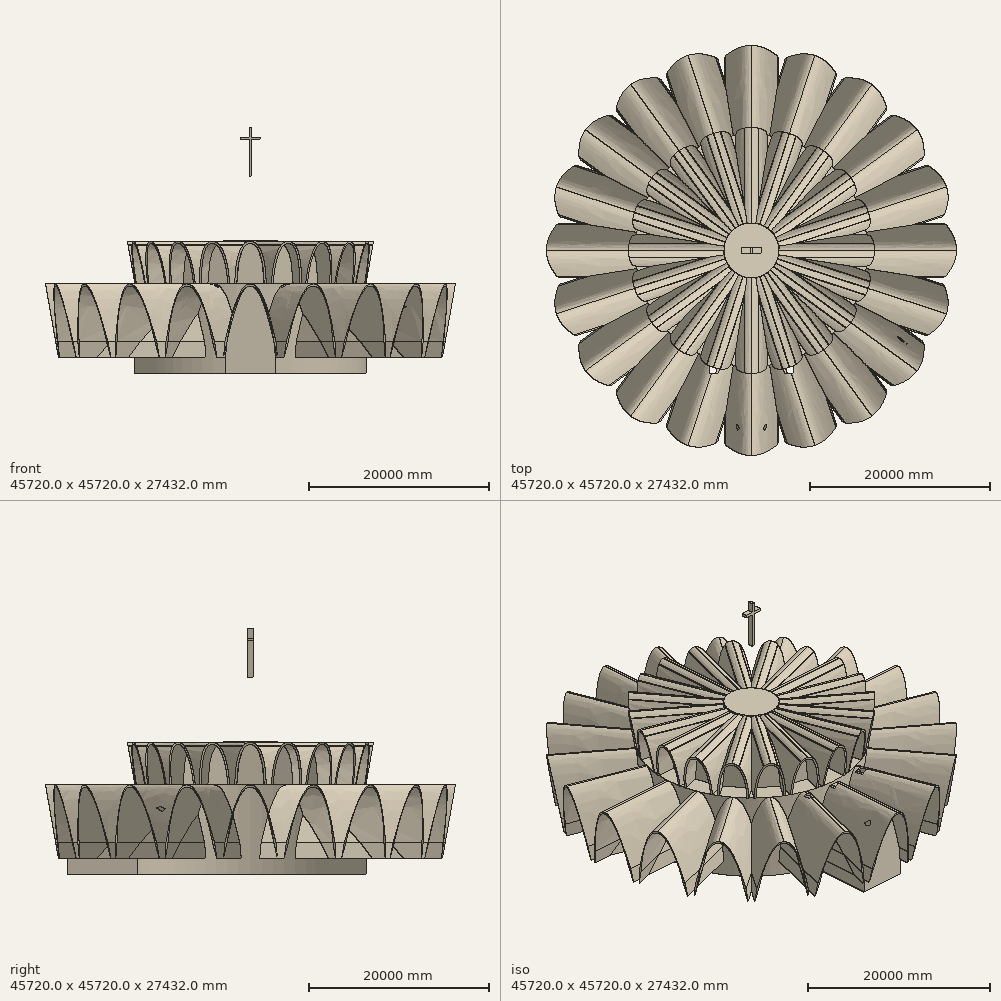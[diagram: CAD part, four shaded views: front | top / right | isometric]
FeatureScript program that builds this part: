
annotation { "Feature Type Name" : "Feature", "Feature Type Description" : "" }
export const myFeature = defineFeature(function(context is Context, id is Id, definition is map)
    precondition{}
    {
        {
            var Q0;
            Q0=qCreatedBy(makeId("Front.planeOp"),FACE);
            var sketch = newSketch(context, id + "F0", { "sketchPlane" : qUnion([Q0])});
            skFitSpline(sketch, "E0", {"points": [v(-2819.4, 0.59) * mm, v(0, 9753.6) * mm, v(3431.03, -271.27) * mm], "startDerivative": vector(-180.02, 33749.09) * mm, "endDerivative": vector(6673.33, -32256.88) * mm});
            skLineSegment(sketch, "E1", {"start": v(0, 0) * mm, "end": v(0, 27432) * mm, "construction": true});
            skFitSpline(sketch, "E2.MirrorCS", {"points": [v(2819.4, 0.59) * mm, v(0, 9753.6) * mm, v(-3431.03, -271.27) * mm], "startDerivative": vector(180.02, 33749.09) * mm, "endDerivative": vector(-6673.33, -32256.88) * mm});
            skLineSegment(sketch, "E3", {"start": v(-1350.09, 27432) * mm, "end": v(1344.94, 27432) * mm, "construction": true});
            skFitSpline(sketch, "E4", {"points": [v(-1524, 9982.83) * mm, v(0, 14487.94) * mm], "startDerivative": vector(0, 6892.9) * mm, "endDerivative": vector(3021.33, 0) * mm});
            skFitSpline(sketch, "E5.MirrorCS", {"points": [v(1524, 9982.83) * mm, v(0, 14487.94) * mm], "startDerivative": vector(0, 6892.9) * mm, "endDerivative": vector(-3021.33, 0) * mm});
            skLineSegment(sketch, "E6", {"start": v(-23096.64, 7972.17) * mm, "end": v(22623.36, 7972.17) * mm, "construction": true});
            skLineSegment(sketch, "E7", {"start": v(-158.94, 27432) * mm, "end": v(-158.94, 26322.91) * mm});
            skLineSegment(sketch, "E8", {"start": v(-158.94, 26322.91) * mm, "end": v(-1101.37, 26322.91) * mm});
            skLineSegment(sketch, "E9", {"start": v(-1101.37, 26322.91) * mm, "end": v(-1101.37, 26041.27) * mm});
            skLineSegment(sketch, "E10", {"start": v(-1101.37, 26041.27) * mm, "end": v(-158.94, 26041.27) * mm});
            skLineSegment(sketch, "E11", {"start": v(-158.94, 26041.27) * mm, "end": v(-158.94, 22529.93) * mm});
            skLineSegment(sketch, "E12.MirrorCS", {"start": v(158.94, 27432) * mm, "end": v(158.94, 26322.91) * mm});
            skLineSegment(sketch, "E13.MirrorCS", {"start": v(158.94, 26322.91) * mm, "end": v(1101.37, 26322.91) * mm});
            skLineSegment(sketch, "E14.MirrorCS", {"start": v(1101.37, 26041.27) * mm, "end": v(158.94, 26041.27) * mm});
            skLineSegment(sketch, "E15.MirrorCS", {"start": v(1101.37, 26322.91) * mm, "end": v(1101.37, 26041.27) * mm});
            skLineSegment(sketch, "E16.MirrorCS", {"start": v(158.94, 26041.27) * mm, "end": v(158.94, 22529.93) * mm});
            skLineSegment(sketch, "E17", {"start": v(-158.94, 27432) * mm, "end": v(0, 27432) * mm});
            skLineSegment(sketch, "E18", {"start": v(0, 27432) * mm, "end": v(158.94, 27432) * mm});
            skFitSpline(sketch, "E19.0", {"points": [v(-3048, -0.63) * mm, v(-3049.89, 353.68) * mm, v(-3040.8, 1051.7) * mm, v(-2991.4, 2062.48) * mm, v(-2909.12, 3032.6) * mm, v(-2796.79, 3957.69) * mm, v(-2657.24, 4833.35) * mm, v(-2493.26, 5655.25) * mm, v(-2307.6, 6419.11) * mm, v(-2137.06, 7003.78) * mm, v(-1992.4, 7438.35) * mm, v(-1880.08, 7747.2) * mm, v(-1764.24, 8038.47) * mm, v(-1645.12, 8311.72) * mm, v(-1522.95, 8566.49) * mm, v(-1397.88, 8802.35) * mm, v(-1270.03, 9018.9) * mm, v(-1161.14, 9182.94) * mm, v(-1072.55, 9304.14) * mm, v(-1005.32, 9389.97) * mm, v(-937.25, 9470.68) * mm, v(-868.26, 9546.2) * mm, v(-798.25, 9616.46) * mm, v(-727.12, 9681.36) * mm, v(-654.72, 9740.78) * mm, v(-580.89, 9794.54) * mm, v(-505.48, 9842.43) * mm, v(-428.34, 9884.14) * mm, v(-349.37, 9919.28) * mm, v(-268.55, 9947.4) * mm, v(-186.02, 9967.95) * mm, v(-116.08, 9978.3) * mm, v(-66.75, 9981.77) * mm, v(-38.5, 9982.66) * mm, v(-17.3, 9982.76) * mm, v(0.38, 9982.39) * mm, v(14.52, 9981.8) * mm, v(35.7, 9980.64) * mm, v(67.38, 9977.86) * mm, v(109.3, 9971.94) * mm, v(150.83, 9963.85) * mm, v(191.87, 9953.68) * mm, v(245.86, 9937.4) * mm, v(311.84, 9912.18) * mm, v(388.4, 9874.73) * mm, v(462.33, 9830.66) * mm, v(533.74, 9780.46) * mm, v(602.85, 9724.5) * mm, v(669.9, 9663.05) * mm, v(735.14, 9596.33) * mm, v(798.8, 9524.48) * mm, v(861.08, 9447.58) * mm, v(922.16, 9365.73) * mm, v(982.2, 9278.98) * mm, v(1061, 9156.85) * mm, v(1157.5, 8992.18) * mm, v(1270.73, 8775.72) * mm, v(1381.87, 8540.78) * mm, v(1491.28, 8287.79) * mm, v(1599.24, 8017.19) * mm, v(1705.95, 7729.47) * mm, v(1811.6, 7425.16) * mm, v(1916.32, 7104.79) * mm, v(2054.9, 6656.96) * mm, v(2226.45, 6059.85) * mm, v(2430.46, 5288.31) * mm, v(2633.35, 4466.59) * mm, v(2835.81, 3599.58) * mm, v(3038.52, 2692.25) * mm, v(3309.96, 1435.38) * mm, v(3515.82, 447.27) * mm, v(3654.89, -224.96) * mm]});
            skLineSegment(sketch, "E20", {"start": v(-23096.64, 7972.17) * mm, "end": v(-22354.3, 1661.45) * mm, "construction": true});
            skLineSegment(sketch, "E21", {"start": v(0, 0) * mm, "end": v(0, -5859.24) * mm, "construction": true});
            skFitSpline(sketch, "E22.0", {"points": [v(3048, -0.63) * mm, v(3049.89, 353.68) * mm, v(3040.8, 1051.7) * mm, v(2991.4, 2062.48) * mm, v(2909.12, 3032.6) * mm, v(2796.79, 3957.69) * mm, v(2657.24, 4833.35) * mm, v(2493.26, 5655.25) * mm, v(2307.6, 6419.11) * mm, v(2137.06, 7003.78) * mm, v(1992.4, 7438.35) * mm, v(1880.08, 7747.2) * mm, v(1764.24, 8038.47) * mm, v(1645.12, 8311.72) * mm, v(1522.95, 8566.49) * mm, v(1397.88, 8802.35) * mm, v(1270.03, 9018.9) * mm, v(1161.14, 9182.94) * mm, v(1072.55, 9304.14) * mm, v(1005.32, 9389.97) * mm, v(937.25, 9470.68) * mm, v(868.26, 9546.2) * mm, v(798.25, 9616.46) * mm, v(727.12, 9681.36) * mm, v(654.72, 9740.78) * mm, v(580.89, 9794.54) * mm, v(505.48, 9842.43) * mm, v(428.34, 9884.14) * mm, v(349.37, 9919.28) * mm, v(268.55, 9947.4) * mm, v(186.02, 9967.95) * mm, v(116.08, 9978.3) * mm, v(66.75, 9981.77) * mm, v(38.5, 9982.66) * mm, v(17.3, 9982.76) * mm, v(-0.38, 9982.39) * mm, v(-14.52, 9981.8) * mm, v(-35.7, 9980.64) * mm, v(-67.38, 9977.86) * mm, v(-109.3, 9971.94) * mm, v(-150.83, 9963.85) * mm, v(-191.87, 9953.68) * mm, v(-245.86, 9937.4) * mm, v(-311.84, 9912.18) * mm, v(-388.4, 9874.73) * mm, v(-462.33, 9830.66) * mm, v(-533.74, 9780.46) * mm, v(-602.85, 9724.5) * mm, v(-669.9, 9663.05) * mm, v(-735.14, 9596.33) * mm, v(-798.8, 9524.48) * mm, v(-861.08, 9447.58) * mm, v(-922.16, 9365.73) * mm, v(-982.2, 9278.98) * mm, v(-1061, 9156.85) * mm, v(-1157.5, 8992.18) * mm, v(-1270.73, 8775.72) * mm, v(-1381.87, 8540.78) * mm, v(-1491.28, 8287.79) * mm, v(-1599.24, 8017.19) * mm, v(-1705.95, 7729.47) * mm, v(-1811.6, 7425.16) * mm, v(-1916.32, 7104.79) * mm, v(-2054.9, 6656.96) * mm, v(-2226.45, 6059.85) * mm, v(-2430.46, 5288.31) * mm, v(-2633.35, 4466.59) * mm, v(-2835.81, 3599.58) * mm, v(-3038.52, 2692.25) * mm, v(-3309.96, 1435.38) * mm, v(-3515.82, 447.27) * mm, v(-3654.89, -224.96) * mm]});
            skLineSegment(sketch, "E23", {"start": v(3048, -0.63) * mm, "end": v(-3048, 0.63) * mm, "construction": true});
            skLineSegment(sketch, "E24", {"start": v(2819.4, 0.59) * mm, "end": v(3048, -0.63) * mm});
            skLineSegment(sketch, "E25", {"start": v(-2819.4, 0.59) * mm, "end": v(-3048, 0.63) * mm});
            skLineSegment(sketch, "E26", {"start": v(-2819.4, 0.59) * mm, "end": v(2819.4, 0.59) * mm});
            skFitSpline(sketch, "E27.0", {"points": [v(-1752.6, 9982.83) * mm, v(-1752.6, 10128.58) * mm, v(-1748.5, 10419.38) * mm, v(-1730.09, 10850.53) * mm, v(-1699.42, 11273.67) * mm, v(-1656.5, 11685.87) * mm, v(-1601.26, 12084.2) * mm, v(-1533.65, 12465.78) * mm, v(-1466.86, 12767.5) * mm, v(-1407.04, 12997.74) * mm, v(-1358.93, 13164.53) * mm, v(-1307.51, 13325.11) * mm, v(-1252.7, 13479.16) * mm, v(-1194.4, 13626.39) * mm, v(-1132.45, 13766.48) * mm, v(-1066.7, 13899.15) * mm, v(-996.9, 14024.1) * mm, v(-922.75, 14141) * mm, v(-843.88, 14249.5) * mm, v(-773.84, 14332.54) * mm, v(-714.95, 14394.24) * mm, v(-669.3, 14438.06) * mm, v(-622.09, 14479.32) * mm, v(-573.26, 14517.88) * mm, v(-522.78, 14553.6) * mm, v(-470.6, 14586.3) * mm, v(-416.75, 14615.8) * mm, v(-361.23, 14641.93) * mm, v(-304.13, 14664.46) * mm, v(-245.56, 14683.2) * mm, v(-185.66, 14697.99) * mm, v(-124.64, 14708.66) * mm, v(-62.7, 14715.1) * mm, v(-20.96, 14716.54) * mm, v(0, 14716.54) * mm]});
            skFitSpline(sketch, "E28.0", {"points": [v(1752.6, 9982.83) * mm, v(1752.6, 10128.58) * mm, v(1748.5, 10419.38) * mm, v(1730.09, 10850.53) * mm, v(1699.42, 11273.67) * mm, v(1656.5, 11685.87) * mm, v(1601.26, 12084.2) * mm, v(1533.65, 12465.78) * mm, v(1466.86, 12767.5) * mm, v(1407.04, 12997.74) * mm, v(1358.93, 13164.53) * mm, v(1307.51, 13325.11) * mm, v(1252.7, 13479.16) * mm, v(1194.4, 13626.39) * mm, v(1132.45, 13766.48) * mm, v(1066.7, 13899.15) * mm, v(996.9, 14024.1) * mm, v(922.75, 14141) * mm, v(843.88, 14249.5) * mm, v(773.84, 14332.54) * mm, v(714.95, 14394.24) * mm, v(669.3, 14438.06) * mm, v(622.09, 14479.32) * mm, v(573.26, 14517.88) * mm, v(522.78, 14553.6) * mm, v(470.6, 14586.3) * mm, v(416.75, 14615.8) * mm, v(361.23, 14641.93) * mm, v(304.13, 14664.46) * mm, v(245.56, 14683.2) * mm, v(185.66, 14697.99) * mm, v(124.64, 14708.66) * mm, v(62.7, 14715.1) * mm, v(20.96, 14716.54) * mm, v(0, 14716.54) * mm]});
            skLineSegment(sketch, "E29", {"start": v(1524, 9982.83) * mm, "end": v(1752.6, 9982.83) * mm});
            skLineSegment(sketch, "E30", {"start": v(-1524, 9982.83) * mm, "end": v(-1752.6, 9982.83) * mm});
            skLineSegment(sketch, "E31", {"start": v(-1524, 9982.83) * mm, "end": v(1524, 9982.83) * mm});
            skFitSpline(sketch, "E32", {"points": [v(-817.81, 14279.49) * mm, v(-6.36, 22529.93) * mm], "startDerivative": vector(515.44, 9073.29) * mm, "endDerivative": vector(1172.76, 164.64) * mm});
            skFitSpline(sketch, "E33.0", {"points": [v(-772.17, 14276.9) * mm, v(-761.43, 14465.95) * mm, v(-739.35, 14860.8) * mm, v(-704.33, 15492.71) * mm, v(-667.33, 16153.61) * mm, v(-628.23, 16832.86) * mm, v(-586.96, 17519.82) * mm, v(-543.4, 18203.85) * mm, v(-497.49, 18874.3) * mm, v(-449.1, 19520.5) * mm, v(-406.64, 20029.92) * mm, v(-371.36, 20414.66) * mm, v(-344.23, 20690.47) * mm, v(-316.41, 20952.2) * mm, v(-287.9, 21198.52) * mm, v(-258.7, 21428.04) * mm, v(-228.8, 21639.43) * mm, v(-198.21, 21831.28) * mm, v(-172.15, 21973.7) * mm, v(-150.98, 22076.44) * mm, v(-134.96, 22147.7) * mm, v(-118.8, 22212.94) * mm, v(-102.54, 22271.97) * mm, v(-86.21, 22324.54) * mm, v(-69.9, 22370.37) * mm, v(-56.43, 22402.67) * mm, v(-45.85, 22424.78) * mm, v(-38.08, 22439.43) * mm, v(-30.55, 22452.08) * mm, v(-23.36, 22462.67) * mm, v(-16.68, 22471.13) * mm, v(-10.72, 22477.42) * mm, v(-6.62, 22480.9) * mm, v(-4.02, 22482.71) * mm, v(-2.44, 22483.65) * mm, v(-1.27, 22484.23) * mm, v(-0.5, 22484.53) * mm, v(-0.08, 22484.64) * mm, v(0, 22484.65) * mm, v(0, 22484.65) * mm]});
            skFitSpline(sketch, "E34.MirrorCS", {"points": [v(817.81, 14279.49) * mm, v(6.36, 22529.93) * mm], "startDerivative": vector(-515.44, 9073.29) * mm, "endDerivative": vector(-1172.76, 164.64) * mm});
            skFitSpline(sketch, "E35.MirrorCS", {"points": [v(817.81, 14279.49) * mm, v(6.36, 22529.93) * mm], "startDerivative": vector(-515.44, 9073.29) * mm, "endDerivative": vector(-1172.76, 164.64) * mm});
            skLineSegment(sketch, "E36", {"start": v(-793.23, 14716.54) * mm, "end": v(793.23, 14716.54) * mm});
            skFitSpline(sketch, "E37.trimOffspring", {"points": [v(772.17, 14276.9) * mm, v(761.43, 14465.95) * mm, v(739.35, 14860.8) * mm, v(704.33, 15492.71) * mm, v(667.33, 16153.61) * mm, v(628.23, 16832.86) * mm, v(586.96, 17519.82) * mm, v(543.4, 18203.85) * mm, v(497.49, 18874.3) * mm, v(449.1, 19520.5) * mm, v(406.64, 20029.92) * mm, v(371.36, 20414.66) * mm, v(344.23, 20690.47) * mm, v(316.41, 20952.2) * mm, v(287.9, 21198.52) * mm, v(258.7, 21428.04) * mm, v(228.8, 21639.43) * mm, v(198.21, 21831.28) * mm, v(172.15, 21973.7) * mm, v(150.98, 22076.44) * mm, v(134.96, 22147.7) * mm, v(118.8, 22212.94) * mm, v(102.54, 22271.97) * mm, v(86.21, 22324.54) * mm, v(69.9, 22370.37) * mm, v(56.43, 22402.67) * mm, v(45.85, 22424.78) * mm, v(38.08, 22439.43) * mm, v(30.55, 22452.08) * mm, v(23.36, 22462.67) * mm, v(16.68, 22471.13) * mm, v(10.72, 22477.42) * mm, v(6.62, 22480.9) * mm, v(4.02, 22482.71) * mm, v(2.44, 22483.65) * mm, v(1.27, 22484.23) * mm, v(0.5, 22484.53) * mm, v(0.08, 22484.64) * mm, v(0, 22484.65) * mm, v(0, 22484.65) * mm]});
            skLineSegment(sketch, "E38", {"start": v(-158.94, 22529.93) * mm, "end": v(158.94, 22529.93) * mm});
            skSolve(sketch);
        }
        {
            var Q0;
            Q0=makeQuery(id+"F0.imprint","IMPRINT",FACE,{"disambiguationData":[TD([[makeQuery(id+"F0.imprint","IMPRINT",EDGE,{"derivedFrom":sQuery(id+"F0.wireOp",EDGE,"E0")}),1.0]])]});
            extrude(context, id + "F1", {"entities" : qUnion([Q0]), "depth" : 22860 * mm, "offsetDistance" : 30.48 * mm});
        }
        {
            var Q0;
            Q0=qCreatedBy(makeId("Right.planeOp"),FACE);
            var sketch = newSketch(context, id + "F2", { "sketchPlane" : qUnion([Q0])});
            skPoint(sketch, "E39.0", {"position": v(-22860, 9982.34) * mm});
            skPoint(sketch, "E40.0", {"position": v(-22860, -208.75) * mm});
            skLineSegment(sketch, "E41", {"start": v(-22860, 9982.34) * mm, "end": v(-21063.03, -208.75) * mm});
            skLineSegment(sketch, "E42", {"start": v(-21063.03, -208.75) * mm, "end": v(-22860, -208.75) * mm});
            skLineSegment(sketch, "E43", {"start": v(-22860, 9982.34) * mm, "end": v(-22860, -208.75) * mm});
            skSolve(sketch);
        }
        {
            var Q0;
            Q0 = qSketchRegion(id + "F2", true);
            extrude(context, id + "F3", {"entities" : qUnion([Q0]), "operationType" : NewBodyOperationType.REMOVE, "oppositeDirection" : true, "depth" : 12192 * mm, "offsetDistance" : 30.48 * mm, "symmetric" : true});
        }
        {
            var Q0;
            Q0=makeQuery(id+"F0.imprint","IMPRINT",FACE,{"disambiguationData":[TD([[makeQuery(id+"F0.imprint","IMPRINT",EDGE,{"derivedFrom":sQuery(id+"F0.wireOp",EDGE,"E0")}),-1.0]])]});
            extrude(context, id + "F4", {"entities" : qUnion([Q0]), "operationType" : NewBodyOperationType.ADD, "depth" : 20421.6 * mm, "offsetDistance" : 30.48 * mm});
        }
        {
            var Q0;
            Q0=makeQuery(id+"F1.opExtrude","SWEPT_BODY",BODY,{"disambiguationData":[OSD([sQuery(id+"F0.wireOp",EDGE,"E0"),sQuery(id+"F0.wireOp",EDGE,"E2.MirrorCS"),sQuery(id+"F0.wireOp",EDGE,"E19.0"),sQuery(id+"F0.wireOp",EDGE,"Ndu0AW5j-bF9E-oolH-Txe2-MfHqacpsOlkU"),sQuery(id+"F0.wireOp",EDGE,"zqyEci1F-S4mj-wNFW-uEhr-tiP0p9dw7OKw"),sQuery(id+"F0.wireOp",EDGE,"E22.0")])]});
            var Q1;
            Q1=sQuery(id+"F0.wireOp",EDGE,"E1");
            circularPattern(context, id + "F5", {"entities" : qUnion([Q0]), "axis" : qUnion([Q1]), "angle" : 360 * degree, "instanceCount" : 20, "equalSpace" : true, "computeTransformsWithoutBuiltin" : true});
        }
        {
            var Q0;
            Q0=makeQuery(id+"F0.imprint","IMPRINT",FACE,{"disambiguationData":[TD([[makeQuery(id+"F0.imprint","IMPRINT",EDGE,{"derivedFrom":sQuery(id+"F0.wireOp",EDGE,"E4")}),1.0]])]});
            extrude(context, id + "F6", {"entities" : qUnion([Q0]), "depth" : 13716 * mm, "offsetDistance" : 30.48 * mm});
        }
        {
            var Q0;
            {var subQ6=sQuery(id+"F0.wireOp",EDGE,"E4");Q0=makeQuery(id+"F0.imprint","IMPRINT",FACE,{"disambiguationData":[TD([[makeQuery(id+"F0.imprint","IMPRINT",EDGE,{"derivedFrom":subQ6}),-1.0]])]});}
            extrude(context, id + "F7", {"entities" : qUnion([Q0]), "depth" : 10668 * mm, "offsetDistance" : 30.48 * mm});
        }
        {
            var Q0;
            Q0=qCreatedBy(makeId("Right.planeOp"),FACE);
            var sketch = newSketch(context, id + "F8", { "sketchPlane" : qUnion([Q0])});
            skPoint(sketch, "E44.0", {"position": v(-13716, 14716.54) * mm});
            skLineSegment(sketch, "E45", {"start": v(-13716, 14716.54) * mm, "end": v(-12816.03, 9612.58) * mm});
            skLineSegment(sketch, "E46", {"start": v(-13716, 14716.54) * mm, "end": v(-13716, 9612.58) * mm});
            skLineSegment(sketch, "E47", {"start": v(-12816.03, 9612.58) * mm, "end": v(-13716, 9612.58) * mm});
            skSolve(sketch);
        }
        {
            var Q0;
            Q0 = qSketchRegion(id + "F8", true);
            extrude(context, id + "F9", {"entities" : qUnion([Q0]), "operationType" : NewBodyOperationType.REMOVE, "oppositeDirection" : true, "depth" : 9326.88 * mm, "offsetDistance" : 30.48 * mm, "symmetric" : true});
        }
        {
            var Q0;
            Q0=makeQuery(id+"F6.opExtrude","SWEPT_BODY",BODY,{"disambiguationData":[OSD([sQuery(id+"F0.wireOp",EDGE,"E4"),sQuery(id+"F0.wireOp",EDGE,"E5.MirrorCS"),sQuery(id+"F0.wireOp",EDGE,"E27.0"),sQuery(id+"F0.wireOp",EDGE,"E28.0"),sQuery(id+"F0.wireOp",EDGE,"E29"),sQuery(id+"F0.wireOp",EDGE,"E30")])]});
            var Q1;
            Q1=makeQuery(id+"F7.opExtrude","SWEPT_BODY",BODY,{"disambiguationData":[OSD([sQuery(id+"F0.wireOp",EDGE,"E4"),sQuery(id+"F0.wireOp",EDGE,"E5.MirrorCS"),sQuery(id+"F0.wireOp",EDGE,"E19.0"),sQuery(id+"F0.wireOp",EDGE,"E22.0"),sQuery(id+"F0.wireOp",EDGE,"E31")])]});
            var Q2;
            Q2=sQuery(id+"F0.wireOp",EDGE,"E1");
            circularPattern(context, id + "F10", {"entities" : qUnion([Q0, Q1]), "axis" : qUnion([Q2]), "angle" : 360 * degree, "instanceCount" : 20, "equalSpace" : true, "computeTransformsWithoutBuiltin" : true});
        }
        {
            var Q0;
            Q0=qCreatedBy(makeId("Top.planeOp"),FACE);
            var sketch = newSketch(context, id + "F11", { "sketchPlane" : qUnion([Q0])});
            skCircle(sketch, "E48", {"center": v(0, 0) * mm, "radius": 12954 * mm});
            skCircle(sketch, "E49", {"center": v(0, 0) * mm, "radius": 3048 * mm});
            skSolve(sketch);
        }
        {
            var Q0;
            Q0 = qSketchRegion(id + "F11", true);
            var Q1;
            Q1=makeQuery(id+"F10.opPattern","COPY",VERTEX,{"derivedFrom":makeQuery(id+"F9.boolean.opBoolean","INTERSECT",VERTEX,{"derivedFrom":[makeQuery(id+"F6.opExtrude","SWEPT_FACE",FACE,{"disambiguationData":[OSD([sQuery(id+"F0.wireOp",EDGE,"E4")])]}),makeQuery(id+"F6.opExtrude","SWEPT_FACE",FACE,{"disambiguationData":[OSD([sQuery(id+"F0.wireOp",EDGE,"E30")])]}),makeQuery(id+"F9.opExtrude","SWEPT_FACE",FACE,{"disambiguationData":[OSD([sQuery(id+"F8.wireOp",EDGE,"E45")])]})]}),"instanceName":"18"});
            extrude(context, id + "F12", {"entities" : qUnion([Q0]), "endBound" : BoundingType.UP_TO_VERTEX, "depth" : 30.48 * mm, "endBoundEntityVertex" : qUnion([Q1]), "offsetDistance" : 30.48 * mm});
        }
        {
            var Q0;
            {var subQ1=sQuery(id+"F0.wireOp",EDGE,"E32");Q0=makeQuery(id+"F0.imprint","IMPRINT",FACE,{"disambiguationData":[TD([[makeQuery(id+"F0.imprint","IMPRINT",EDGE,{"derivedFrom":subQ1}),-1.0]])]});}
            var Q1;
            {var subQ0=sQuery(id+"F0.wireOp",EDGE,"E33.0");Q1=makeQuery(id+"F0.imprint","IMPRINT",FACE,{"disambiguationData":[TD([[makeQuery(id+"F0.imprint","IMPRINT",EDGE,{"derivedFrom":subQ0}),-1.0]])]});}
            extrude(context, id + "F13", {"entities" : qUnion([Q0, Q1]), "depth" : 3048 * mm, "offsetDistance" : 30.48 * mm});
        }
        {
            var Q0;
            Q0=makeQuery(id+"F11.imprint","IMPRINT",FACE,{"disambiguationData":[TD([[makeQuery(id+"F11.imprint","IMPRINT",EDGE,{"derivedFrom":sQuery(id+"F11.wireOp",EDGE,"E49")}),1.0]])]});
            extrude(context, id + "F14", {"entities" : qUnion([Q0]), "depth" : 14782.8 * mm, "offsetDistance" : 30.48 * mm});
        }
        {
            var Q0;
            Q0=makeQuery(id+"F13.opExtrude","SWEPT_BODY",BODY,{"disambiguationData":[OSD([sQuery(id+"F0.wireOp",EDGE,"E32"),sQuery(id+"F0.wireOp",EDGE,"E33.0"),sQuery(id+"F0.wireOp",EDGE,"E35.MirrorCS"),sQuery(id+"F0.wireOp",EDGE,"E36"),sQuery(id+"F0.wireOp",EDGE,"E37.trimOffspring")])]});
            var Q1;
            Q1=sQuery(id+"F0.wireOp",EDGE,"E1");
            circularPattern(context, id + "F15", {"entities" : qUnion([Q0]), "axis" : qUnion([Q1]), "angle" : 360 * degree, "instanceCount" : 10, "equalSpace" : true, "computeTransformsWithoutBuiltin" : true});
        }
        {
            var Q0;
            Q0=makeQuery(id+"F0.imprint","IMPRINT",FACE,{"disambiguationData":[TD([[makeQuery(id+"F0.imprint","IMPRINT",EDGE,{"derivedFrom":sQuery(id+"F0.wireOp",EDGE,"E7")}),1.0]])]});
            extrude(context, id + "F16", {"entities" : qUnion([Q0]), "depth" : 609.6 * mm, "offsetDistance" : 30.48 * mm, "symmetric" : true});
        }
        {
            var Q0;
            Q0=makeQuery(id+"F16.opExtrude","SWEPT_FACE",FACE,{"disambiguationData":[OSD([sQuery(id+"F0.wireOp",EDGE,"E38")])]});
            var sketch = newSketch(context, id + "F17", { "sketchPlane" : qUnion([Q0])});
            skLineSegment(sketch, "E50.bottom", {"start": v(-158.94, 304.8) * mm, "end": v(158.94, 304.8) * mm});
            skLineSegment(sketch, "E50.top", {"start": v(-158.94, -304.8) * mm, "end": v(158.94, -304.8) * mm});
            skLineSegment(sketch, "E50.left", {"start": v(-158.94, 304.8) * mm, "end": v(-158.94, -304.8) * mm});
            skLineSegment(sketch, "E50.right", {"start": v(158.94, 304.8) * mm, "end": v(158.94, -304.8) * mm});
            skSolve(sketch);
        }
        {
            var Q0;
            Q0 = qSketchRegion(id + "F17", true);
            extrude(context, id + "F18", {"entities" : qUnion([Q0]), "operationType" : NewBodyOperationType.ADD, "depth" : 521.2 * mm, "offsetDistance" : 30.48 * mm});
        }
    });
